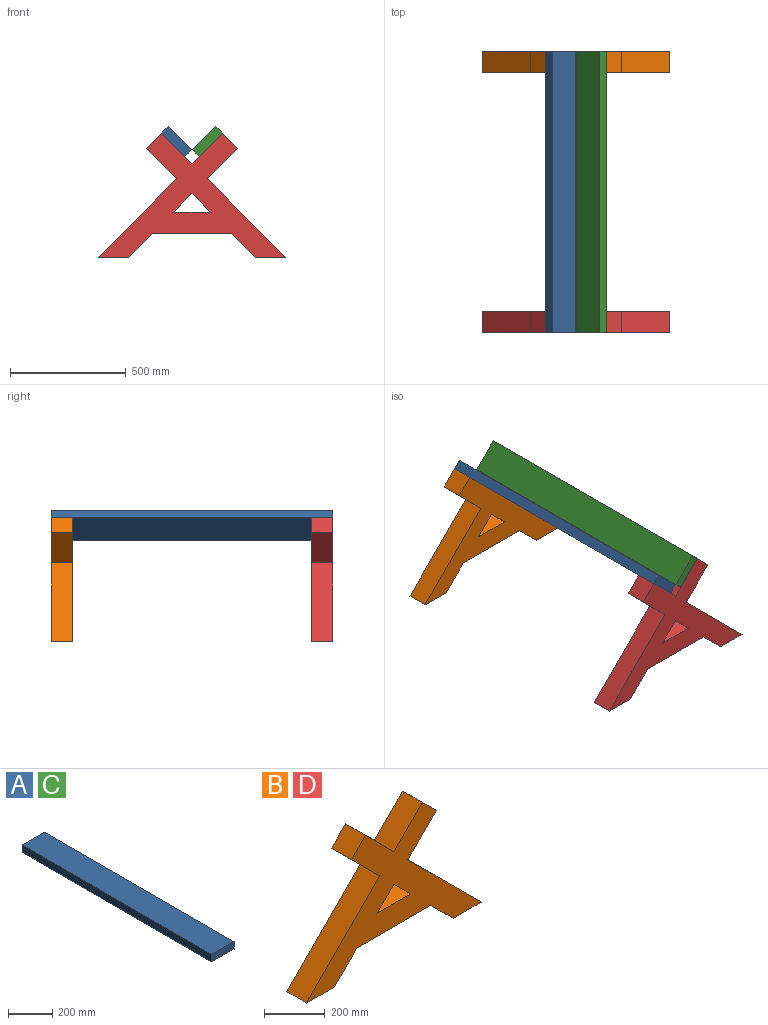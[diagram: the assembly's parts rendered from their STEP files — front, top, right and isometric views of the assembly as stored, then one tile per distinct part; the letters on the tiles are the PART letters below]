
ASSEMBLY  parts=4 mates=9
PART A: 6 faces, bbox 142.9x1219.2x41.3 mm
  f0: plane 1219.2x41.28mm, normal (-1,0,0), area 50322.5mm2, adj f1,f3,f4,f5
  f1: plane 1219.2x142.88mm, normal (0,0,-1), area 174193.2mm2, adj f0,f2,f4,f5
  f2: plane 1219.2x41.28mm, normal (1,0,0), area 50322.5mm2, adj f1,f3,f4,f5
  f3: plane 1219.2x142.88mm, normal (0,0,1), area 174193.2mm2, adj f0,f2,f4,f5
  f4: plane 142.88x41.28mm, normal (0,-1,0), area 5897.2mm2, adj f0,f1,f2,f3
  f5: plane 142.88x41.28mm, normal (0,1,0), area 5897.2mm2, adj f0,f1,f2,f3
PART B: 18 faces, bbox 812.8x92.1x538.8 mm
  f0: plane 92.08x79.38mm, normal (-0.71,0,-0.71), area 10335.7mm2, adj f1,f15,f16,f17
  f1: plane 158.75x92.08mm, normal (0,0,1), area 14616.9mm2, adj f0,f15,f16,f17
  f2: plane 132.42x132.42mm, normal (0.71,0,0.71), area 17242.3mm2, adj f3,f14,f16,f17
  f3: plane 92.08x65.11mm, normal (-0.71,0,0.71), area 8477.8mm2, adj f2,f4,f16,f17
  f4: plane 132.42x132.42mm, normal (-0.71,0,-0.71), area 17242.3mm2, adj f3,f5,f16,f17
  f5: plane 341.29x341.29mm, normal (-0.71,0,0.71), area 44441mm2, adj f4,f6,f16,f17
  f6: plane 130.21x92.08mm, normal (0,0,-1), area 11989.4mm2, adj f5,f7,f16,f17
  f7: plane 104.74x104.74mm, normal (0.71,0,-0.71), area 13638.1mm2, adj f6,f8,f16,f17
  f8: plane 342.9x92.08mm, normal (0,0,-1), area 31572.5mm2, adj f7,f9,f16,f17
  f9: plane 104.74x104.74mm, normal (-0.71,0,-0.71), area 13638.1mm2, adj f8,f10,f16,f17
  f10: plane 130.21x92.08mm, normal (0,0,-1), area 11989.4mm2, adj f9,f11,f16,f17
  f11: plane 341.29x341.29mm, normal (0.71,0,0.71), area 44441mm2, adj f10,f12,f16,f17
  f12: plane 132.42x132.42mm, normal (0.71,0,-0.71), area 17242.3mm2, adj f11,f13,f16,f17
  f13: plane 92.08x65.11mm, normal (0.71,0,0.71), area 8477.8mm2, adj f12,f14,f16,f17
  f14: plane 132.42x132.42mm, normal (-0.71,0,0.71), area 17242.3mm2, adj f2,f13,f16,f17
  f15: plane 92.08x79.38mm, normal (0.71,0,-0.71), area 10335.7mm2, adj f0,f1,f16,f17
  f16: plane 812.8x538.82mm, normal (0,-1,0), area 146461.4mm2, adj f0,f1,f2,f3,f4,f5,f6,f7
  f17: plane 812.8x538.82mm, normal (0,1,0), area 146461.4mm2, adj f0,f1,f2,f3,f4,f5,f6,f7
PART C: same geometry as A
PART D: same geometry as B
PLACE A rot(axis=(0,1,0),45deg) t=(143.77,1219.2,538.82)mm
PLACE B t=(276.19,1219.2,0)mm
PLACE C rot(axis=(0,-1,0),45deg) t=(307.57,1219.2,437.79)mm
PLACE D t=(276.19,92.07,0)mm
MATE planar D.f3 <-> A.f0  axis (-0.71,0,0.71) through (111.22,46.04,506.26)mm
MATE planar C.f2 <-> D.f13  axis (0.71,0,0.71) through (394.01,609.6,553.41)mm
MATE planar B.f1 <-> D.f1  axis (0,0,1) through (276.19,1173.16,196.81)mm
MATE planar B.f17 <-> C.f5  axis (0,1,0) through (276.19,1219.2,231.31)mm
MATE planar D.f2 <-> A.f1  axis (0.71,0,0.71) through (209.98,46.04,472.61)mm
MATE planar D.f16 <-> A.f4  axis (0,-1,0) through (276.19,0,231.31)mm
MATE planar C.f4 <-> D.f16  axis (0,-1,0) through (343.49,0,502.89)mm
MATE planar B.f2 <-> A.f1  axis (0.71,0,0.71) through (209.98,1173.16,472.61)mm
MATE planar C.f1 <-> D.f14  axis (0.71,0,-0.71) through (358.09,609.6,488.3)mm
